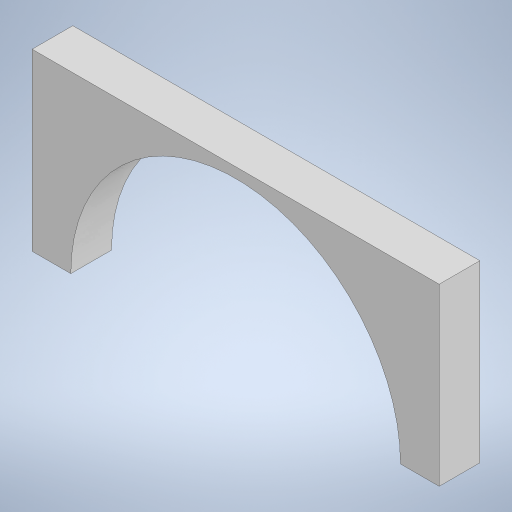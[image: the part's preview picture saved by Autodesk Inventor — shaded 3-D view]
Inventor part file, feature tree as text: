
AUTODESK INVENTOR PART (.ipt)
format: ipt  version: 2023 (Build 270158000, 158)  size: 226,304 bytes
history: native  units: mm
features: extrude x2, sketch x2
ambient origin geometry x8: Origin, YZ Plane, XZ Plane, XY Plane, X Axis, Y Axis, Z Axis, Center Point
bodies: Body1 (feature_tree)
feature tree (4):
  extrude  "Extrusion11"  Depth=43.0mm
  extrude  "Extrusion12"  Depth=50.0mm
  sketch  "Sketch13"  dims[d42=100.0mm d43=43.0mm]
  sketch  "Sketch14"  dims[d44=10.0mm d45=0.0mm d46=81.0mm d47=50.0mm d48=0.0mm d49=0.5mm d50=0.872665mm d51=0.5mm d52=0.872665mm]
